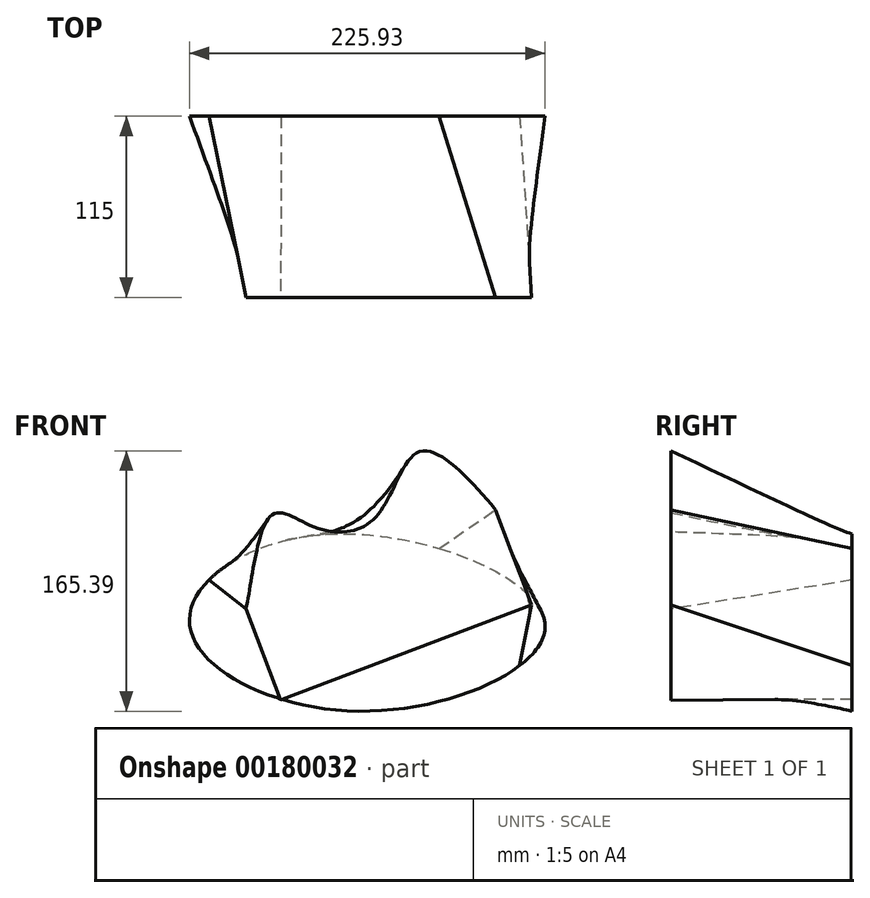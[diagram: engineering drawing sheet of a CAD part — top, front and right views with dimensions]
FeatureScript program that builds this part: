
annotation { "Feature Type Name" : "Feature", "Feature Type Description" : "" }
export const myFeature = defineFeature(function(context is Context, id is Id, definition is map)
    precondition{}
    {
        {
            var Q0;
            Q0=qCreatedBy(makeId("Front.planeOp"),FACE);
            var sketch = newSketch(context, id + "F0", { "sketchPlane" : qUnion([Q0])});
            skFitSpline(sketch, "E0", {"points": [v(-108.6, 0) * mm, v(-23.34, 56.98) * mm, v(117.15, 0) * mm, v(0, -55.32) * mm, v(-108.6, 0) * mm]});
            skSolve(sketch);
        }
        {
            var Q0;
            Q0=qCreatedBy(makeId("Front.planeOp"),FACE);
            cPlane(context, id + "F1", {"entities" : qUnion([Q0]), "cplaneType" : CPlaneType.OFFSET, "offset" : 115 * mm, "width" : 150 * mm, "height" : 150 * mm});
        }
        {
            var Q0;
            Q0=qCreatedBy(id+"F1.planeOp",FACE);
            var sketch = newSketch(context, id + "F2", { "sketchPlane" : qUnion([Q0])});
            skLineSegment(sketch, "E1.top", {"start": v(-50.7, -48.33) * mm, "end": v(108.73, 12.2) * mm});
            skLineSegment(sketch, "E1.left", {"start": v(-72.7, 9.61) * mm, "end": v(-50.7, -48.33) * mm});
            skLineSegment(sketch, "E1.right", {"start": v(85.79, 72.63) * mm, "end": v(108.73, 12.2) * mm});
            skFitSpline(sketch, "E2", {"points": [v(-72.7, 9.61) * mm, v(-56.31, 69.33) * mm, v(-29.45, 61.72) * mm, v(9.26, 67.6) * mm, v(37.3, 109.5) * mm, v(85.79, 72.63) * mm], "startDerivative": vector(50.49, 231.11) * mm, "endDerivative": vector(214.6, -255.65) * mm});
            skSolve(sketch);
        }
        {
            var Q0;
            Q0 = qSketchRegion(id + "F0", true);
            var Q1;
            Q1 = qSketchRegion(id + "F2", true);
            loft(context, id + "F3", {"sheetProfilesArray" : [{ "sheetProfileEntities" : qUnion([Q0]) }, { "sheetProfileEntities" : qUnion([Q1]) }]});
        }
    });
